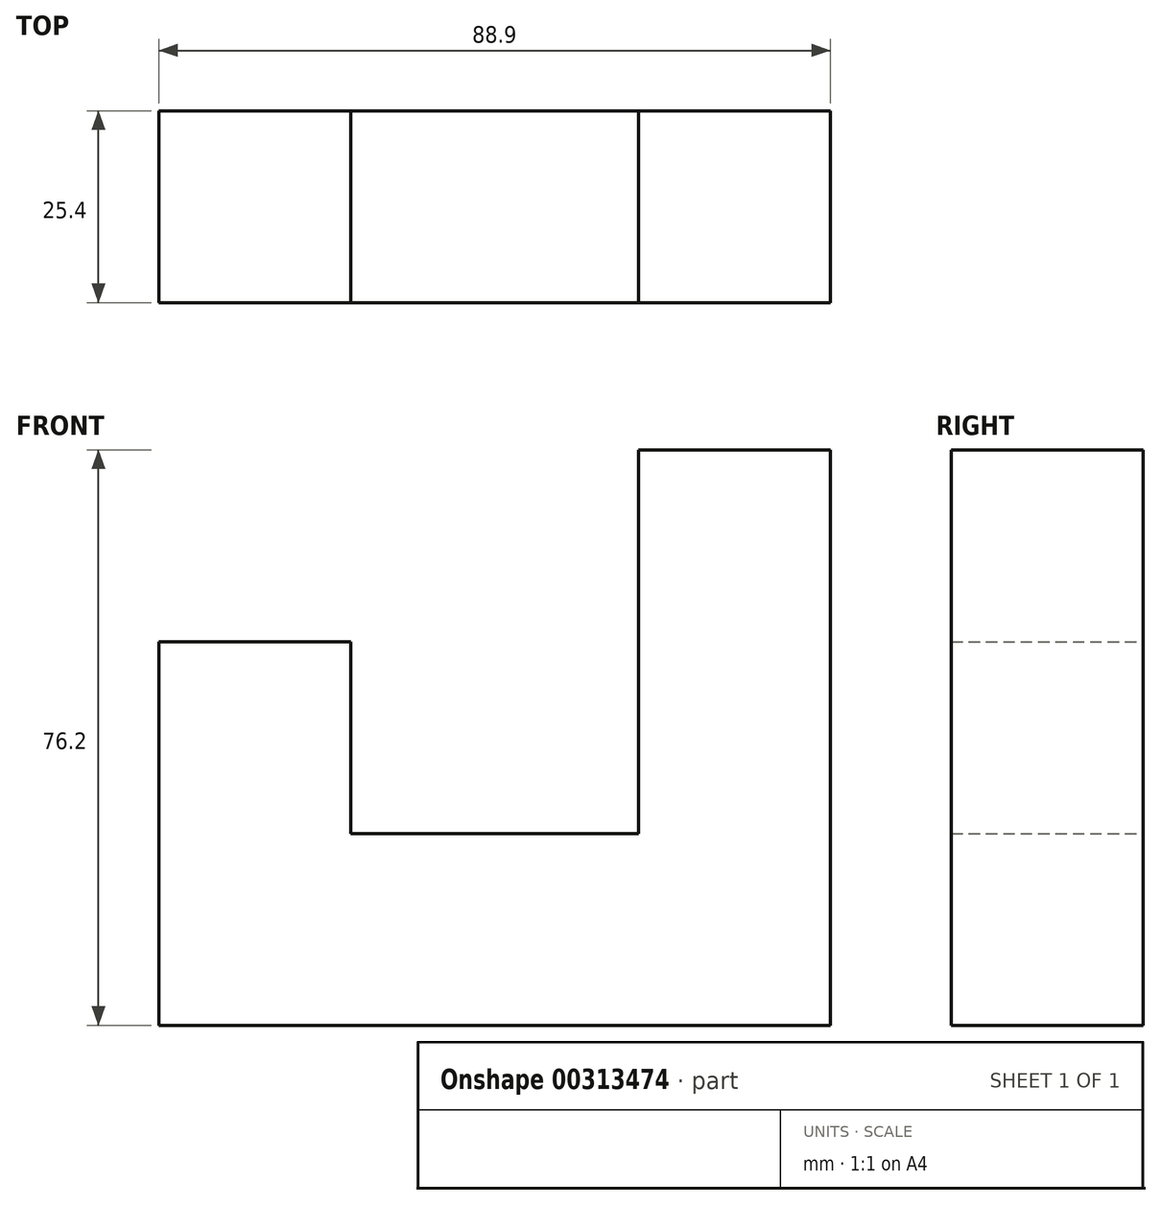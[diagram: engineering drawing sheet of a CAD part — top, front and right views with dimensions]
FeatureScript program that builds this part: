
annotation { "Feature Type Name" : "Feature", "Feature Type Description" : "" }
export const myFeature = defineFeature(function(context is Context, id is Id, definition is map)
    precondition{}
    {
        {
            var Q0;
            Q0=qCreatedBy(makeId("Front.planeOp"),FACE);
            var sketch = newSketch(context, id + "F0", { "sketchPlane" : qUnion([Q0])});
            skLineSegment(sketch, "E0", {"start": v(-41.23, -36.13) * mm, "end": v(47.67, -36.13) * mm});
            skLineSegment(sketch, "E1", {"start": v(47.67, -36.13) * mm, "end": v(47.67, 40.07) * mm});
            skLineSegment(sketch, "E2", {"start": v(47.67, 40.07) * mm, "end": v(22.27, 40.07) * mm});
            skLineSegment(sketch, "E3", {"start": v(22.27, 40.07) * mm, "end": v(22.27, -10.73) * mm});
            skLineSegment(sketch, "E4", {"start": v(22.27, -10.73) * mm, "end": v(-15.83, -10.73) * mm});
            skLineSegment(sketch, "E5", {"start": v(-15.83, -10.73) * mm, "end": v(-15.83, 14.67) * mm});
            skLineSegment(sketch, "E6", {"start": v(-15.83, 14.67) * mm, "end": v(-41.23, 14.67) * mm});
            skLineSegment(sketch, "E7", {"start": v(-41.23, 14.67) * mm, "end": v(-41.23, -36.13) * mm});
            skSolve(sketch);
        }
        {
            var Q0;
            Q0=makeQuery(id+"F0.imprint","IMPRINT",FACE,{"disambiguationData":[TD([[makeQuery(id+"F0.imprint","IMPRINT",EDGE,{"derivedFrom":sQuery(id+"F0.wireOp",EDGE,"E0")}),1.0]])]});
            extrude(context, id + "F1", {"entities" : qUnion([Q0]), "depth" : 25.4 * mm});
        }
    });
